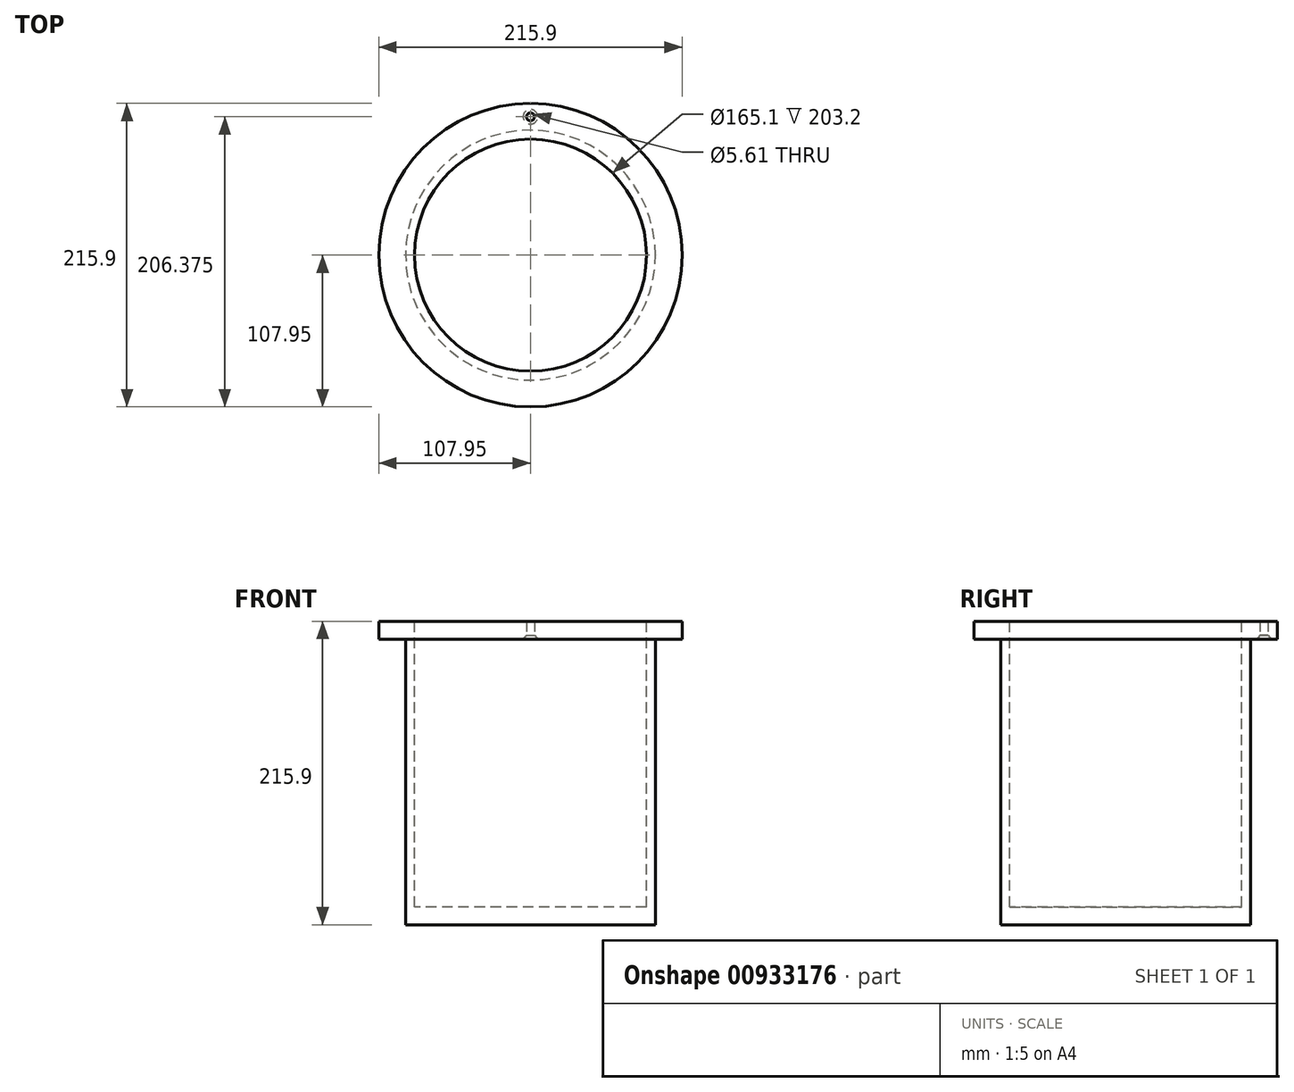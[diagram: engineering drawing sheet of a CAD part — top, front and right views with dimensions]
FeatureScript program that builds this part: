
annotation { "Feature Type Name" : "Feature", "Feature Type Description" : "" }
export const myFeature = defineFeature(function(context is Context, id is Id, definition is map)
    precondition{}
    {
        {
            var Q0;
            Q0=qCreatedBy(makeId("Top.planeOp"),FACE);
            var sketch = newSketch(context, id + "F0", { "sketchPlane" : qUnion([Q0])});
            skCircle(sketch, "E0", {"center": v(0, 0) * mm, "radius": 107.95 * mm});
            skSolve(sketch);
        }
        {
            var Q0;
            Q0=makeQuery(id+"F0.imprint","IMPRINT",FACE,{"disambiguationData":[TD([[makeQuery(id+"F0.imprint","IMPRINT",EDGE,{"derivedFrom":sQuery(id+"F0.wireOp",EDGE,"E0")}),1.0]])]});
            var Q1;
            Q1=sQuery(id+"F0.wireOp",EDGE,"E0");
            extrude(context, id + "F1", {"entities" : qUnion([Q0]), "surfaceEntities" : qUnion([Q1]), "oppositeDirection" : true, "depth" : 12.7 * mm, "offsetDistance" : 25.4 * mm});
        }
        {
            var Q0;
            Q0=makeQuery(id+"F1.opExtrude","CAP_FACE",FACE,{"disambiguationData":[OSD([sQuery(id+"F0.wireOp",EDGE,"E0")])],"isStart":false});
            var sketch = newSketch(context, id + "F2", { "sketchPlane" : qUnion([Q0])});
            skCircle(sketch, "E1", {"center": v(0, 0) * mm, "radius": 88.9 * mm});
            skSolve(sketch);
        }
        {
            var Q0;
            Q0 = qSketchRegion(id + "F2", true);
            extrude(context, id + "F3", {"entities" : qUnion([Q0]), "operationType" : NewBodyOperationType.ADD, "depth" : 203.2 * mm, "offsetDistance" : 25.4 * mm});
        }
        {
            var Q0;
            Q0=makeQuery(id+"F1.opExtrude","CAP_FACE",FACE,{"disambiguationData":[OSD([sQuery(id+"F0.wireOp",EDGE,"E0")])],"isStart":true});
            var sketch = newSketch(context, id + "F4", { "sketchPlane" : qUnion([Q0])});
            skCircle(sketch, "E2", {"center": v(0, 0) * mm, "radius": 82.55 * mm});
            skSolve(sketch);
        }
        {
            var Q0;
            Q0=makeQuery(id+"F4.imprint","IMPRINT",FACE,{"disambiguationData":[TD([[makeQuery(id+"F4.imprint","IMPRINT",EDGE,{"derivedFrom":sQuery(id+"F4.wireOp",EDGE,"E2")}),1.0]])]});
            extrude(context, id + "F5", {"entities" : qUnion([Q0]), "operationType" : NewBodyOperationType.REMOVE, "oppositeDirection" : true, "depth" : 203.2 * mm, "offsetDistance" : 25.4 * mm});
        }
        {
            var Q0;
            Q0=makeQuery(id+"F1.opExtrude","CAP_FACE",FACE,{"disambiguationData":[OSD([sQuery(id+"F0.wireOp",EDGE,"E0")])],"isStart":false});
            var sketch = newSketch(context, id + "F6", { "sketchPlane" : qUnion([Q0])});
            skPoint(sketch, "E3", {"position": v(0, -98.43) * mm});
            skSolve(sketch);
        }
        {
            var Q0;
            Q0=sQuery(id+"F6.wireOp",VERTEX,"E3");
            var Q1;
            Q1=makeQuery(id+"F1.opExtrude","SWEPT_BODY",BODY,{"disambiguationData":[OSD([sQuery(id+"F0.wireOp",EDGE,"E0")])]});
            hole(context, id + "F7", {"style" : HoleStyle.C_SINK, "endStyle" : HoleEndStyle.THROUGH, "standardTappedOrClearance" : lookupTablePath({ "fit" : "Normal (ASME)", "standard" : "ANSI", "size" : "#10", "type" : "Clearance" }), "standardBlindInLast" : lookupTablePath({ "fit" : "Normal", "standard" : "ANSI", "engagement" : "75%", "pitch" : "24 tpi", "size" : "#10", "type" : "Clearance & tapped" }), "holeDiameter" : 5.61 * mm, "cSinkDiameter" : 10.44 * mm, "cSinkAngle" : 82 * degree, "majorDiameter" : 6.35 * mm, "isTappedThrough" : true, "tappedDepth" : 12.7 * mm, "tapClearance" : 3, "locations" : qUnion([Q0]), "scope" : qUnion([Q1])});
        }
    });
